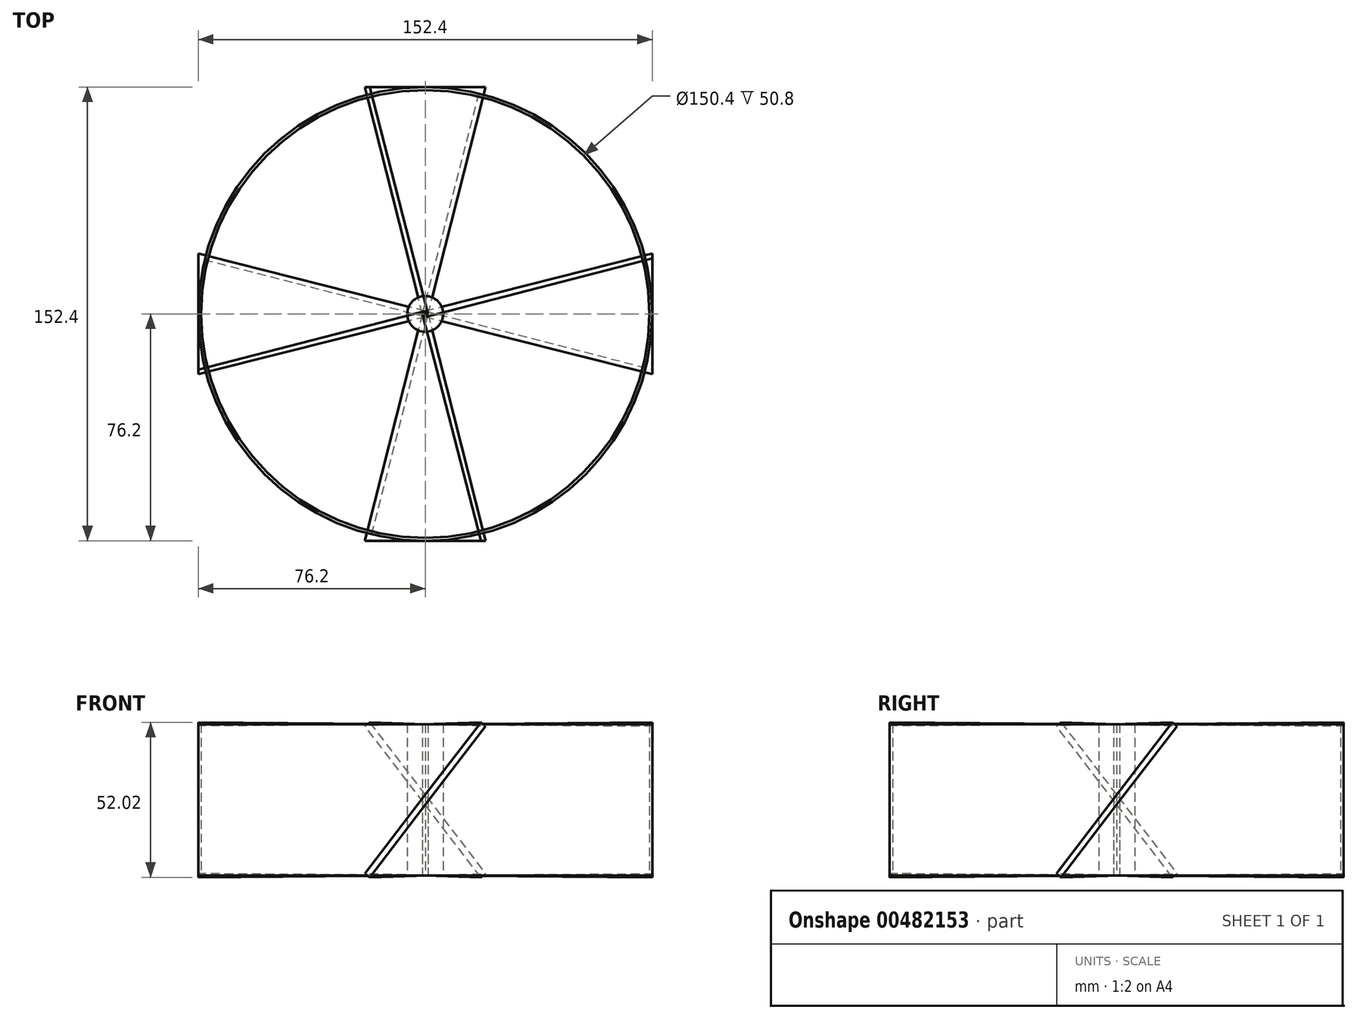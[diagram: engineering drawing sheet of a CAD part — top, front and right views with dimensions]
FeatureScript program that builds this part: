
annotation { "Feature Type Name" : "Feature", "Feature Type Description" : "" }
export const myFeature = defineFeature(function(context is Context, id is Id, definition is map)
    precondition{}
    {
        {
            var Q0;
            Q0=qCreatedBy(makeId("Top.planeOp"),FACE);
            var sketch = newSketch(context, id + "F0", { "sketchPlane" : qUnion([Q0])});
            skCircle(sketch, "E0", {"center": v(0, 0) * mm, "radius": 76.2 * mm});
            skCircle(sketch, "E1", {"center": v(0, 0) * mm, "radius": 75.2 * mm});
            skSolve(sketch);
        }
        {
            var Q0;
            Q0 = qSketchRegion(id + "F0", true);
            extrude(context, id + "F1", {"entities" : qUnion([Q0]), "depth" : 50.8 * mm});
        }
        {
            var Q0;
            Q0=qCreatedBy(makeId("Top.planeOp"),FACE);
            var sketch = newSketch(context, id + "F2", { "sketchPlane" : qUnion([Q0])});
            skLineSegment(sketch, "E2", {"start": v(0, 0) * mm, "end": v(0, 75.2) * mm});
            skSolve(sketch);
        }
        {
            var Q0;
            Q0=qCreatedBy(makeId("Top.planeOp"),FACE);
            var sketch = newSketch(context, id + "F3", { "sketchPlane" : qUnion([Q0])});
            skArc(sketch, "E3", {"start": v(-5.8, 1.55) * mm, "mid": v(-6, 0) * mm, "end": v(-5.8, -1.55) * mm});
            skLineSegment(sketch, "E4", {"start": v(-5.8, -1.55) * mm, "end": v(-72.64, -19.46) * mm});
            skLineSegment(sketch, "E5", {"start": v(-5.8, 1.55) * mm, "end": v(-72.64, 19.46) * mm});
            skLineSegment(sketch, "E6", {"start": v(0, 0) * mm, "end": v(-75.2, 0) * mm, "construction": true});
            skArc(sketch, "E7", {"start": v(-72.64, 19.46) * mm, "mid": v(-75.2, 0) * mm, "end": v(-72.64, -19.46) * mm});
            skPoint(sketch, "E7.third.point", {"position": v(74.68, 8.83) * mm});
            skSolve(sketch);
        }
        {
            var Q0;
            Q0=qCreatedBy(makeId("Right.planeOp"),FACE);
            var sketch = newSketch(context, id + "F4", { "sketchPlane" : qUnion([Q0])});
            skLineSegment(sketch, "E8", {"start": v(0, 0) * mm, "end": v(0, 62) * mm, "construction": true});
            skSolve(sketch);
        }
        {
            var Q0;
            Q0=qCreatedBy(makeId("Right.planeOp"),FACE);
            cPlane(context, id + "F5", {"entities" : qUnion([Q0]), "cplaneType" : CPlaneType.OFFSET, "offset" : 76.2 * mm, "oppositeDirection" : true, "width" : 150 * mm, "height" : 150 * mm});
        }
        {
            var Q0;
            Q0=qCreatedBy(id+"F5.planeOp",FACE);
            var sketch = newSketch(context, id + "F6", { "sketchPlane" : qUnion([Q0])});
            skLineSegment(sketch, "E9", {"start": v(19.46, 0) * mm, "end": v(-19.46, 50.8) * mm, "construction": true});
            skLineSegment(sketch, "E10", {"start": v(-18.67, 51.4) * mm, "end": v(20.26, 0.6) * mm});
            skLineSegment(sketch, "E11", {"start": v(20.26, 0.6) * mm, "end": v(18.67, -0.6) * mm});
            skLineSegment(sketch, "E12", {"start": v(18.67, -0.6) * mm, "end": v(-20.26, 50.2) * mm});
            skLineSegment(sketch, "E13", {"start": v(-20.26, 50.2) * mm, "end": v(-18.67, 51.4) * mm});
            skSolve(sketch);
        }
        {
            var Q0;
            Q0=qCreatedBy(makeId("Right.planeOp"),FACE);
            var sketch = newSketch(context, id + "F7", { "sketchPlane" : qUnion([Q0])});
            skLineSegment(sketch, "E14.bottom", {"start": v(1, 50.8) * mm, "end": v(-1, 50.8) * mm});
            skLineSegment(sketch, "E14.top", {"start": v(1, 0) * mm, "end": v(-1, 0) * mm});
            skLineSegment(sketch, "E14.left", {"start": v(1, 50.8) * mm, "end": v(1, 0) * mm});
            skLineSegment(sketch, "E14.right", {"start": v(-1, 50.8) * mm, "end": v(-1, 0) * mm});
            skPoint(sketch, "E14.middle", {"position": v(0, 25.4) * mm});
            skSolve(sketch);
        }
        {
            var Q0;
            Q0=makeQuery(id+"F7.imprint","IMPRINT",FACE,{"disambiguationData":[TD([[makeQuery(id+"F7.imprint","IMPRINT",EDGE,{"derivedFrom":sQuery(id+"F7.wireOp",EDGE,"E14.bottom")}),1.0]])]});
            var Q1;
            Q1=makeQuery(id+"F6.imprint","IMPRINT",FACE,{"disambiguationData":[TD([[makeQuery(id+"F6.imprint","IMPRINT",EDGE,{"derivedFrom":sQuery(id+"F6.wireOp",EDGE,"E10")}),-1.0]])]});
            loft(context, id + "F8", {"sheetProfilesArray" : [{ "sheetProfileEntities" : qUnion([Q0]) }, { "sheetProfileEntities" : qUnion([Q1]) }]});
        }
        {
            var Q0;
            Q0=makeQuery(id+"F8.opLoft","SWEPT_BODY",BODY,{"disambiguationData":[OSD([makeQuery(id+"F6.imprint","IMPRINT",FACE,{"disambiguationData":[TD([[makeQuery(id+"F6.imprint","IMPRINT",EDGE,{"derivedFrom":sQuery(id+"F6.wireOp",EDGE,"E10")}),-1.0]])]}),makeQuery(id+"F7.imprint","IMPRINT",FACE,{"disambiguationData":[TD([[makeQuery(id+"F7.imprint","IMPRINT",EDGE,{"derivedFrom":sQuery(id+"F7.wireOp",EDGE,"E14.bottom")}),1.0]])]})])]});
            var Q1;
            Q1=sQuery(id+"F4.wireOp",EDGE,"E8");
            circularPattern(context, id + "F9", {"entities" : qUnion([Q0]), "axis" : qUnion([Q1]), "angle" : 360 * degree, "instanceCount" : 4, "equalSpace" : true});
        }
        {
            var Q0;
            Q0=qCreatedBy(makeId("Top.planeOp"),FACE);
            var sketch = newSketch(context, id + "F10", { "sketchPlane" : qUnion([Q0])});
            skCircle(sketch, "E15", {"center": v(0, 0) * mm, "radius": 6 * mm});
            skSolve(sketch);
        }
        {
            var Q0;
            Q0 = qSketchRegion(id + "F10", true);
            var Q1;
            Q1=makeQuery(id+"F1.opExtrude","CAP_FACE",FACE,{"disambiguationData":[OSD([sQuery(id+"F0.wireOp",EDGE,"E0"),sQuery(id+"F0.wireOp",EDGE,"E1")])],"isStart":false});
            extrude(context, id + "F11", {"entities" : qUnion([Q0]), "endBound" : BoundingType.UP_TO_SURFACE, "endBoundEntityFace" : qUnion([Q1]), "depth" : 25 * mm});
        }
        {
            var Q0;
            Q0 = qSketchRegion(id + "F2", true);
            var Q1;
            Q1=makeQuery(id+"F1.opExtrude","CAP_FACE",FACE,{"disambiguationData":[OSD([sQuery(id+"F0.wireOp",EDGE,"E0"),sQuery(id+"F0.wireOp",EDGE,"E1")])],"isStart":false});
            var Q2;
            Q2=sQuery(id+"F2.wireOp",EDGE,"E2");
            var Q3;
            Q3=makeQuery(id+"F1.opExtrude","CAP_FACE",FACE,{"disambiguationData":[OSD([sQuery(id+"F0.wireOp",EDGE,"E0"),sQuery(id+"F0.wireOp",EDGE,"E1")])],"isStart":false});
            extrude(context, id + "F12", {"entities" : qUnion([Q0, Q1]), "bodyType" : ToolBodyType.SURFACE, "surfaceEntities" : qUnion([Q2]), "endBound" : BoundingType.UP_TO_SURFACE, "endBoundEntityFace" : qUnion([Q3]), "depth" : 25 * mm});
        }
        {
            var Q0;
            Q0=makeQuery(id+"F12.opExtrude","SWEPT_BODY",BODY,{"disambiguationData":[OSD([sQuery(id+"F2.wireOp",EDGE,"E2")])]});
            var Q1;
            Q1=sQuery(id+"F4.wireOp",EDGE,"E8");
            circularPattern(context, id + "F13", {"entities" : qUnion([Q0]), "axis" : qUnion([Q1]), "angle" : 360 * degree, "instanceCount" : 4, "equalSpace" : true});
        }
    });
